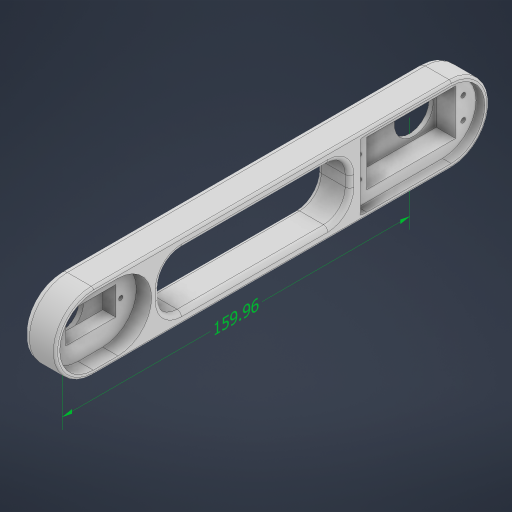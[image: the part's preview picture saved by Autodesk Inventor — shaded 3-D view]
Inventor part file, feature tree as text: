
AUTODESK INVENTOR PART (.ipt)
format: ipt  version: 2023 (Build 270158000, 158)  size: 387,072 bytes
history: native  units: mm
features: extrude x10, sketch x10, fillet x7, thread x6, other x2
ambient origin geometry x8: Origin, YZ Plane, XZ Plane, XY Plane, X Axis, Y Axis, Z Axis, Center Point
bodies: Solid1 (feature_tree)
feature tree (35):
  other  "Annotations"
  extrude  "Extrusion1"  Depth=200.0mm
  fillet  "Fillet1"  Radius=15.0mm
  fillet  "Fillet2"  Radius=17.5mm
  extrude  "Extrusion2"  Depth=4.0mm TaperAngle=0.0deg
  extrude  "Extrusion3"  Depth=21.0mm
  extrude  "Extrusion4"  Depth=9.0mm
  extrude  "Extrusion5"  Depth=2.0mm TaperAngle=0.0deg
  thread  "Thread1"  [1 undecoded]
  thread  "Thread2"  [1 undecoded]
  thread  "Thread3"  [1 undecoded]
  thread  "Thread4"  [1 undecoded]
  extrude  "Extrusion6"  Depth=2.2mm
  extrude  "Extrusion7"  Depth=3.5mm
  extrude  "Extrusion8"  Depth=10.0mm TaperAngle=0.0deg
  extrude  "Extrusion9"  Depth=10.0mm TaperAngle=0.0deg
  thread  "Thread5"  [1 undecoded]
  thread  "Thread6"  [1 undecoded]
  extrude  "Extrusion11"  Depth=23.0mm
  fillet  "Fillet4"  Radius=13.0mm
  fillet  "Fillet5"  Radius=6.0mm
  fillet  "Fillet6"  Radius=15.0mm
  fillet  "Fillet7"  Radius=6.5mm
  fillet  "Fillet8"  Radius=6.0mm
  sketch  "Sketch1"  dims[d0=35.0mm d1=200.0mm d2=15.0mm d3=0.0mm d4=17.5mm]
  sketch  "Sketch2"  dims[d5=17.5mm d7=4.0mm d8=0.0mm]
  sketch  "Sketch3"  dims[d14=41.0mm d15=21.0mm]
  sketch  "Sketch4"  dims[d16=9.0mm d17=0.0mm d18=18.0mm]
  sketch  "Sketch5"  dims[d19=10.25mm d20=2.0mm d21=0.0mm d29=2.2mm d30=3.5mm d31=2.2mm d32=3.5mm]
  sketch  "Sketch6"  dims[d33=2.2mm d34=2.2mm]
  sketch  "Sketch7"  dims[d35=3.5mm d36=3.5mm]
  sketch  "Sketch8"  dims[d37=10.0mm d38=0.0mm d39=10.0mm d40=0.0mm]
  sketch  "Sketch9"  dims[d41=10.0mm d42=0.0mm d43=10.0mm d44=0.0mm d45=10.0mm d46=0.0mm d47=31.0mm]
  sketch  "Sketch11"  dims[d48=7.0mm d49=0.0mm d50=23.0mm d51=13.0mm d52=6.0mm d53=0.0mm d54=15.0mm d55=6.5mm d56=6.0mm d57=0.0mm d58=2.0mm d59=2.0mm d60=2.3mm d61=2.3mm d62=6.0mm d63=0.0mm d64=6.0mm d65=0.0mm d66=6.0mm d67=0.0mm d73=5.0mm d74=5.0mm d75=5.0mm d76=15.0mm d77=0.0mm d78=10.0mm d79=3.0mm d80=1.0mm d81=2.0mm d82=2.0mm d83=159.956128mm]
  other  "Linear Dimension 1"
note: 6 required parameter values undecoded (feature->parameter linkage not recoverable at this tier; creation-order binding heuristic only, values carry confidence <= 0.55)
